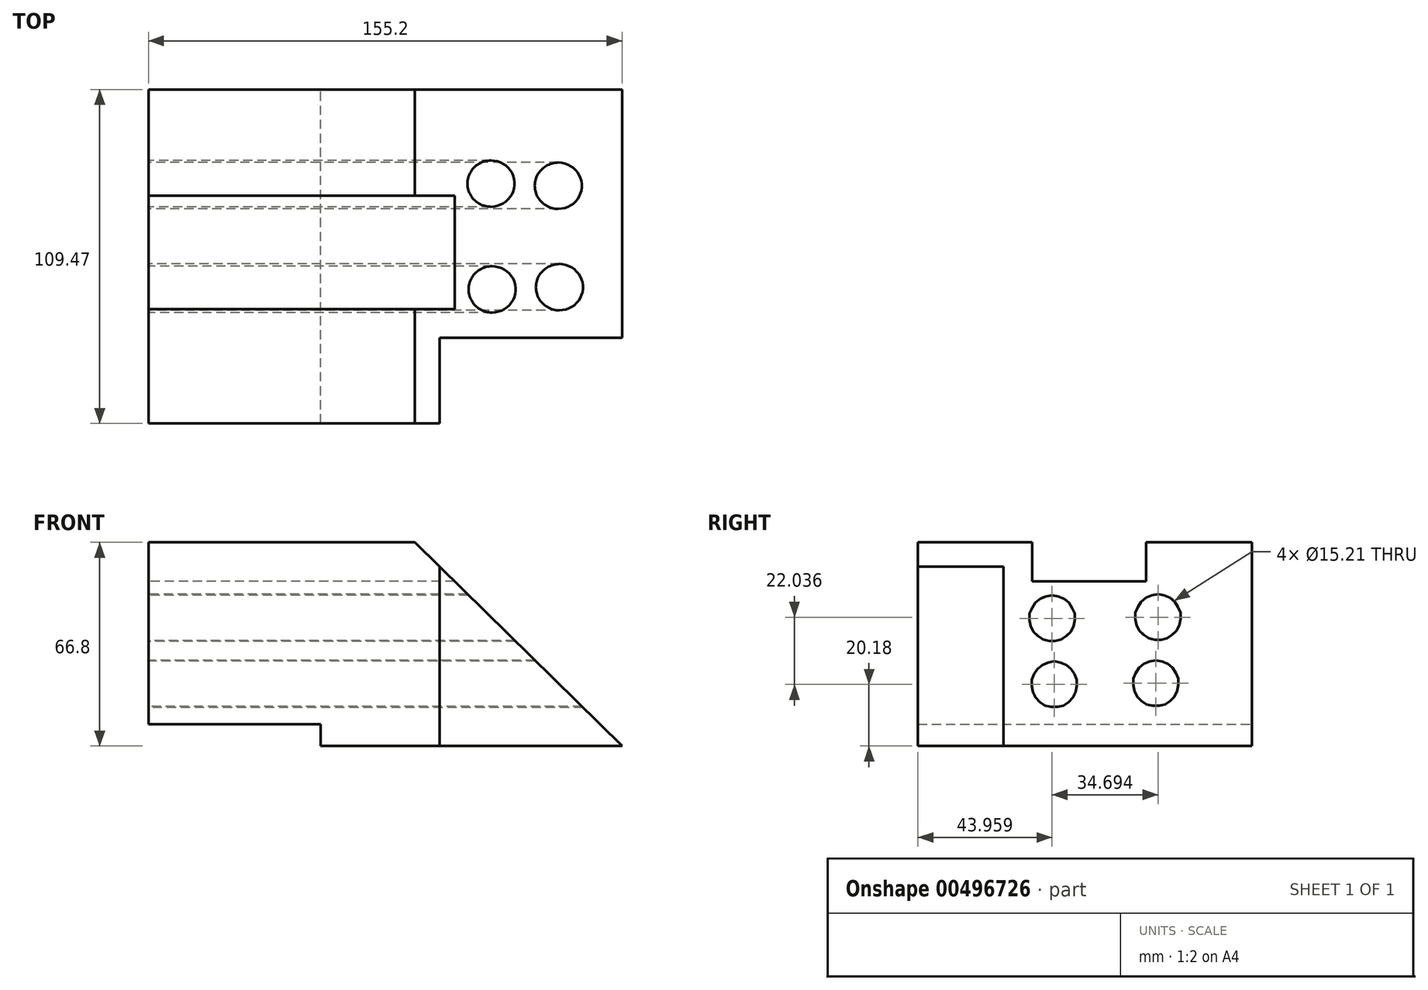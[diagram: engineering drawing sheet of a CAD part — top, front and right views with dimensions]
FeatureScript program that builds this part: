
annotation { "Feature Type Name" : "Feature", "Feature Type Description" : "" }
export const myFeature = defineFeature(function(context is Context, id is Id, definition is map)
    precondition{}
    {
        {
            var Q0;
            Q0=qCreatedBy(makeId("Front.planeOp"),FACE);
            var sketch = newSketch(context, id + "F0", { "sketchPlane" : qUnion([Q0])});
            skLineSegment(sketch, "E0", {"start": v(-48.03, 0) * mm, "end": v(-48.03, 66.8) * mm});
            skLineSegment(sketch, "E1", {"start": v(-48.03, 66.8) * mm, "end": v(39.22, 66.8) * mm});
            skLineSegment(sketch, "E2", {"start": v(39.22, 66.8) * mm, "end": v(107.17, 0) * mm});
            skLineSegment(sketch, "E3", {"start": v(107.17, 0) * mm, "end": v(-48.03, 0) * mm});
            skSolve(sketch);
        }
        {
            var Q0;
            Q0=makeQuery(id+"F0.imprint","IMPRINT",FACE,{"disambiguationData":[TD([[makeQuery(id+"F0.imprint","IMPRINT",EDGE,{"derivedFrom":sQuery(id+"F0.wireOp",EDGE,"E0")}),-1.0]])]});
            extrude(context, id + "F1", {"entities" : qUnion([Q0]), "depth" : 109.47 * mm});
        }
        {
            var Q0;
            Q0=makeQuery(id+"F1.opExtrude","SWEPT_FACE",FACE,{"disambiguationData":[OSD([sQuery(id+"F0.wireOp",EDGE,"E0")])]});
            var sketch = newSketch(context, id + "F2", { "sketchPlane" : qUnion([Q0])});
            skLineSegment(sketch, "E4.bottom", {"start": v(34.73, 66.8) * mm, "end": v(72.04, 66.8) * mm});
            skLineSegment(sketch, "E4.top", {"start": v(34.73, 53.94) * mm, "end": v(72.04, 53.94) * mm});
            skLineSegment(sketch, "E4.left", {"start": v(34.73, 66.8) * mm, "end": v(34.73, 53.94) * mm});
            skLineSegment(sketch, "E4.right", {"start": v(72.04, 66.8) * mm, "end": v(72.04, 53.94) * mm});
            skCircle(sketch, "E5", {"center": v(30.82, 42.22) * mm, "radius": 7.6 * mm});
            skCircle(sketch, "E6", {"center": v(31.53, 20.54) * mm, "radius": 7.6 * mm});
            skCircle(sketch, "E7.MirrorC", {"center": v(64.8, 20.18) * mm, "radius": 7.6 * mm});
            skCircle(sketch, "E8.MirrorC", {"center": v(65.51, 41.86) * mm, "radius": 7.6 * mm});
            skSolve(sketch);
        }
        {
            var Q0;
            Q0=qSketchRegion(id+"F2",true);
            extrude(context, id + "F3", {"entities" : qUnion([Q0]), "operationType" : NewBodyOperationType.REMOVE, "endBound" : BoundingType.THROUGH_ALL, "oppositeDirection" : true, "depth" : 25.4 * mm});
        }
        {
            var Q0;
            Q0=makeQuery(id+"F1.opExtrude","SWEPT_FACE",FACE,{"disambiguationData":[OSD([sQuery(id+"F0.wireOp",EDGE,"E3")])]});
            var sketch = newSketch(context, id + "F4", { "sketchPlane" : qUnion([Q0])});
            skLineSegment(sketch, "E9.bottom", {"start": v(107.17, 109.47) * mm, "end": v(47.36, 109.47) * mm});
            skLineSegment(sketch, "E9.top", {"start": v(107.17, 81.43) * mm, "end": v(47.36, 81.43) * mm});
            skLineSegment(sketch, "E9.left", {"start": v(107.17, 109.47) * mm, "end": v(107.17, 81.43) * mm});
            skLineSegment(sketch, "E9.right", {"start": v(47.36, 109.47) * mm, "end": v(47.36, 81.43) * mm});
            skSolve(sketch);
        }
        {
            var Q0;
            Q0=makeQuery(id+"F4.imprint","IMPRINT",FACE,{"disambiguationData":[TD([[makeQuery(id+"F4.imprint","IMPRINT",EDGE,{"derivedFrom":sQuery(id+"F4.wireOp",EDGE,"E9.bottom")}),1.0]])]});
            extrude(context, id + "F5", {"entities" : qUnion([Q0]), "operationType" : NewBodyOperationType.REMOVE, "endBound" : BoundingType.THROUGH_ALL, "oppositeDirection" : true, "depth" : 25.4 * mm});
        }
        {
            var Q0;
            Q0=makeQuery(id+"F1.opExtrude","SWEPT_FACE",FACE,{"disambiguationData":[OSD([sQuery(id+"F0.wireOp",EDGE,"E3")])]});
            var sketch = newSketch(context, id + "F6", { "sketchPlane" : qUnion([Q0])});
            skLineSegment(sketch, "E10.bottom", {"start": v(-48.03, 109.47) * mm, "end": v(8.37, 109.47) * mm});
            skLineSegment(sketch, "E10.top", {"start": v(-48.03, 0) * mm, "end": v(8.37, 0) * mm});
            skLineSegment(sketch, "E10.left", {"start": v(-48.03, 109.47) * mm, "end": v(-48.03, 0) * mm});
            skLineSegment(sketch, "E10.right", {"start": v(8.37, 109.47) * mm, "end": v(8.37, 0) * mm});
            skSolve(sketch);
        }
        {
            var Q0;
            Q0=makeQuery(id+"F6.imprint","IMPRINT",FACE,{"disambiguationData":[TD([[makeQuery(id+"F6.imprint","IMPRINT",EDGE,{"derivedFrom":sQuery(id+"F6.wireOp",EDGE,"E10.bottom")}),1.0]])]});
            extrude(context, id + "F7", {"entities" : qUnion([Q0]), "operationType" : NewBodyOperationType.REMOVE, "oppositeDirection" : true, "depth" : 7.11 * mm});
        }
    });
